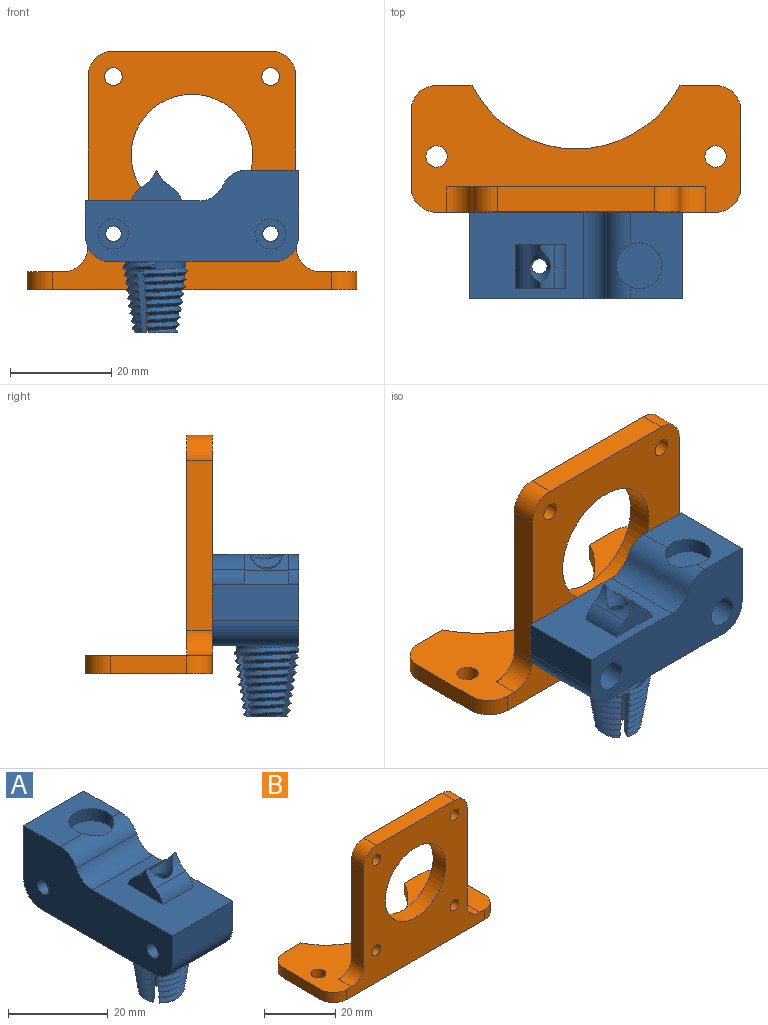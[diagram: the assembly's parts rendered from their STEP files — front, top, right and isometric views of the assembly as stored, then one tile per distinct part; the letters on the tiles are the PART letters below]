
ASSEMBLY  parts=2 mates=1
PART A: 93 faces, bbox 17.4x42.2x32.9 mm
  f0: plane 22.5x17mm, normal (0,0,1), area 296.5mm2, adj f61,f64,f66,f69,f72,f73,f85,f91
  f1: bspline ~12.95x12.81mm, area 38.6mm2, adj f2,f6,f9,f25,f76,f77,f78,f81
  f2: bspline ~12.93x12.82mm, area 52.3mm2, adj f1,f6,f40,f60,f79,f80,f81,f83
  f3: plane 32x17mm, normal (0,0,-1), area 430.9mm2, adj f7,f8,f60,f66,f85
  f4: cylinder r=3mm len=7mm, axis (1,0,0), area 131.9mm2, adj f67,f85
  f5: cylinder r=3mm len=7mm, axis (1,0,0), area 131.9mm2, adj f68,f85
  f6: plane 1.5x0.55mm, normal (0,1,0), area 0.4mm2, adj f1,f2,f60,f86
  f7: cylinder r=5mm len=17mm, axis (-1,0,0), area 133.5mm2, adj f3,f64,f66,f85
  f8: cylinder r=5mm len=17mm, axis (1,0,0), area 133.5mm2, adj f3,f65,f66,f85
  f9: bspline ~8.42x5.37mm, area 10.7mm2, adj f1,f33,f78,f81
  f10: bspline ~10.47x7.65mm, area 10.2mm2, adj f33,f34,f78,f81
  f11: bspline ~11.25x9.09mm, area 9.7mm2, adj f34,f35,f78,f81
  f12: bspline ~9.94x6.45mm, area 9.2mm2, adj f35,f36,f78,f81
  f13: bspline ~8.41x7.9mm, area 8.7mm2, adj f36,f37,f78,f81
  f14: bspline ~6.62x4.21mm, area 8.2mm2, adj f37,f38,f78,f81
  f15: bspline ~7.95x6.8mm, area 7.7mm2, adj f38,f39,f78,f81
  f16: bspline ~7.75x7.69mm, area 5.2mm2, adj f39,f57,f78,f81
  f17: bspline ~12.25x7.86mm, area 10.5mm2, adj f40,f41,f80,f83
  f18: bspline ~11.43x5.71mm, area 10mm2, adj f41,f42,f80,f83
  f19: bspline ~8.73x2.48mm, area 9.5mm2, adj f42,f43,f80,f83
  f20: bspline ~10.76x6.9mm, area 9mm2, adj f43,f44,f80,f83
  f21: bspline ~10.16x4.53mm, area 8.5mm2, adj f44,f45,f80,f83
  f22: bspline ~9.79x5.76mm, area 8mm2, adj f45,f46,f80,f83
  f23: bspline ~9.22x3.92mm, area 7.5mm2, adj f46,f47,f80,f83
  f24: bspline ~5.06x1.51mm, area 1mm2, adj f47,f58,f80
  f25: bspline ~12.58x9.49mm, area 10.8mm2, adj f1,f48,f77,f84
  f26: bspline ~10.93x7.22mm, area 10.3mm2, adj f48,f49,f77,f84
  f27: bspline ~7.78x5.02mm, area 9.8mm2, adj f49,f50,f77,f84
  f28: bspline ~9.75x7.21mm, area 9.3mm2, adj f50,f51,f77,f84
  f29: bspline ~10.36x8.84mm, area 8.8mm2, adj f51,f52,f77,f84
  f30: bspline ~8.65x7.04mm, area 8.3mm2, adj f52,f53,f77,f84
  f31: bspline ~9.22x8.3mm, area 7.8mm2, adj f53,f54,f77,f84
  f32: bspline ~7.52x6.72mm, area 7.3mm2, adj f54,f55,f77,f84
  f33: bspline ~8.42x5.4mm, area 10.5mm2, adj f9,f10,f78,f81
  f34: bspline ~8.06x5.17mm, area 10mm2, adj f10,f11,f78,f81
  f35: bspline ~7.7x4.94mm, area 9.5mm2, adj f11,f12,f78,f81
  f36: bspline ~7.34x4.71mm, area 9mm2, adj f12,f13,f78,f81
  f37: bspline ~6.98x4.47mm, area 8.5mm2, adj f13,f14,f78,f81
  f38: bspline ~6.62x4.24mm, area 8mm2, adj f14,f15,f78,f81
  f39: bspline ~6.26x4.01mm, area 7.5mm2, adj f15,f16,f78,f81
  f40: bspline ~9.97x2.98mm, area 10.8mm2, adj f2,f17,f80,f83
  f41: bspline ~9.56x2.86mm, area 10.3mm2, adj f17,f18,f80,f83
  f42: bspline ~9.14x2.75mm, area 9.8mm2, adj f18,f19,f80,f83
  f43: bspline ~8.73x2.63mm, area 9.3mm2, adj f19,f20,f80,f83
  f44: bspline ~8.31x2.52mm, area 8.8mm2, adj f20,f21,f80,f83
  f45: bspline ~7.9x2.4mm, area 8.3mm2, adj f21,f22,f80,f83
  f46: bspline ~7.48x2.29mm, area 7.8mm2, adj f22,f23,f80,f83
  f47: bspline ~7.06x2.18mm, area 7.3mm2, adj f23,f24,f58,f80,f83
  f48: bspline ~8.5x5.52mm, area 10.7mm2, adj f25,f26,f77,f84
  f49: bspline ~8.14x5.29mm, area 10.2mm2, adj f26,f27,f77,f84
  f50: bspline ~7.78x5.05mm, area 9.7mm2, adj f27,f28,f77,f84
  f51: bspline ~7.42x4.82mm, area 9.1mm2, adj f28,f29,f77,f84
  f52: bspline ~7.06x4.59mm, area 8.6mm2, adj f29,f30,f77,f84
  f53: bspline ~6.7x4.36mm, area 8.2mm2, adj f30,f31,f77,f84
  f54: bspline ~6.34x4.13mm, area 7.6mm2, adj f31,f32,f77,f84
  f55: bspline ~7.52x6.72mm, area 3.3mm2, adj f32,f59,f77,f84
  f56: cylinder r=2.2mm len=26mm, axis (0,0,1), area 304.3mm2, adj f57,f58,f59,f75,f76,f77,f78,f79
  f57: plane 5.91x3.58mm, normal (0,0,-1), area 11mm2, adj f16,f56,f78,f81
  f58: plane 6.05x2.29mm, normal (0,0,-1), area 8.2mm2, adj f24,f47,f56,f80,f83
  f59: plane 5.6x3.29mm, normal (0,0,-1), area 10.1mm2, adj f55,f56,f77,f84
  f60: cone r=6mm half-angle=9deg, axis (0,0,1), area 28.2mm2, adj f2,f3,f6
  f61: plane 10x6mm, normal (1,0,0), area 30.3mm2, adj f0,f70,f71,f72,f73
  f62: cylinder r=1.55mm len=10mm, axis (-1,0,0), area 97.4mm2, adj f66,f68
  f63: cylinder r=1.55mm len=10mm, axis (-1,0,0), area 97.4mm2, adj f66,f67
  f64: plane 17x7mm, normal (0,-1,0), area 119mm2, adj f0,f7,f66,f85
  f65: plane 17x13mm, normal (0,1,0), area 221mm2, adj f8,f66,f85,f88
  f66: plane 42x18mm, normal (-1,0,0), area 567.7mm2, adj f0,f3,f7,f8,f62,f63,f64,f65
  f67: plane 6x6mm, normal (1,0,0), area 20.7mm2, adj f4,f63
  f68: plane 6x6mm, normal (1,0,0), area 20.7mm2, adj f5,f62
  f69: plane 10x6mm, normal (-1,0,0), area 30.3mm2, adj f0,f70,f71,f72,f73
  f70: cylinder r=6.85mm len=8.6mm, axis (1,0,0), area 21.4mm2, adj f61,f69,f71,f73,f87
  f71: cylinder r=6.36mm len=8.6mm, axis (1,0,0), area 19.7mm2, adj f61,f69,f70,f72,f87
  f72: cylinder r=5mm len=8.6mm, axis (1,0,0), area 31.5mm2, adj f0,f61,f69,f71
  f73: cylinder r=5mm len=8.6mm, axis (1,0,0), area 31.8mm2, adj f0,f61,f69,f70
  f74: cylinder r=1.5mm len=3mm, axis (0,0,-1), area 18.8mm2, adj f75,f87
  f75: plane 4.4x4.4mm, normal (0,0,-1), area 8.1mm2, adj f56,f74
  f76: plane 4.26x1.51mm, normal (0,0,-1), area 6.2mm2, adj f1,f56,f77,f78
  f77: plane 12.02x4.19mm, normal (1,0,0), area 35.4mm2, adj f1,f25,f26,f27,f28,f29,f30,f31
  f78: plane 12.02x4.25mm, normal (-1,0,0), area 35.4mm2, adj f1,f9,f10,f11,f12,f13,f14,f15
  f79: plane 4.12x3.23mm, normal (0,0,-1), area 5.7mm2, adj f2,f56,f80,f81
  f80: plane 12.02x3.62mm, normal (0.5,0.87,0), area 35.5mm2, adj f2,f17,f18,f19,f20,f21,f22,f23
  f81: plane 12.02x3.63mm, normal (-0.5,-0.87,0), area 35.5mm2, adj f1,f2,f9,f10,f11,f12,f13,f14
  f82: plane 3.97x3.13mm, normal (0,0,-1), area 5.4mm2, adj f1,f56,f83,f84
  f83: plane 12.02x3.56mm, normal (-0.5,0.87,0), area 35.4mm2, adj f1,f2,f17,f18,f19,f20,f21,f22
  f84: plane 12.02x3.55mm, normal (0.5,-0.87,0), area 35.4mm2, adj f1,f25,f26,f27,f28,f29,f30,f31
  f85: plane 42x18mm, normal (1,0,0), area 526.2mm2, adj f0,f3,f4,f5,f7,f8,f64,f65
  f86: plane 1.9x0.78mm, normal (1,0,0), area 0.6mm2, adj f1,f2,f6
  f87: cone r=1.5mm half-angle=25deg, axis (0,0,1), area 27mm2, adj f70,f71,f74
  f88: plane 17x10.34mm, normal (0,0,1), area 128.2mm2, adj f65,f66,f85,f89,f92
  f89: cylinder r=4.5mm len=9mm, axis (0,0,1), area 84.8mm2, adj f88,f90,f92
  f90: plane 9x9mm, normal (0,0,1), area 63.6mm2, adj f89
  f91: cylinder r=5mm len=17mm, axis (1,0,0), area 98.5mm2, adj f0,f66,f85,f92
  f92: cylinder r=5mm len=17mm, axis (1,0,0), area 81.8mm2, adj f66,f85,f88,f89,f91
PART B: 29 faces, bbox 65x25x47 mm
  f0: plane 33.5x5mm, normal (-1,0,0), area 167.5mm2, adj f2,f5,f19,f25
  f1: plane 33.5x5mm, normal (1,0,0), area 167.5mm2, adj f2,f5,f20,f26
  f2: plane 51x43.5mm, normal (0,1,0), area 1292.6mm2, adj f0,f1,f3,f6,f7,f8,f9,f10
  f3: plane 31x5mm, normal (0,0,1), area 155mm2, adj f2,f5,f25,f26
  f4: plane 65x25mm, normal (0,0,-1), area 1209.6mm2, adj f5,f12,f13,f14,f15,f16,f17,f18
  f5: plane 55x47mm, normal (0,-1,0), area 1485.1mm2, adj f0,f1,f3,f4,f6,f7,f8,f9
  f6: cylinder r=12mm len=24mm, axis (0,-1,0), area 377mm2, adj f2,f5
  f7: cylinder r=1.75mm len=5mm, axis (0,-1,0), area 55mm2, adj f2,f5
  f8: cylinder r=1.75mm len=5mm, axis (0,-1,0), area 55mm2, adj f2,f5
  f9: cylinder r=1.75mm len=5mm, axis (0,-1,0), area 55mm2, adj f2,f5
  f10: cylinder r=1.75mm len=5mm, axis (0,-1,0), area 55mm2, adj f2,f5
  f11: plane 65x25mm, normal (0,0,1), area 954.6mm2, adj f2,f5,f12,f13,f14,f15,f16,f17
  f12: plane 15x3.5mm, normal (1,0,0), area 52.5mm2, adj f4,f11,f23,f24
  f13: plane 15x3.5mm, normal (-1,0,0), area 52.5mm2, adj f4,f11,f21,f22
  f14: plane 7x3.5mm, normal (0,1,0), area 24.5mm2, adj f4,f11,f17,f22
  f15: plane 3.5x0.07mm, normal (0,1,0), area 0.3mm2, adj f4,f11,f17,f18
  f16: plane 7x3.5mm, normal (0,1,0), area 24.5mm2, adj f4,f11,f18,f23
  f17: cylinder r=23mm len=20.46mm, axis (0,0,1), area 88.3mm2, adj f4,f11,f14,f15
  f18: cylinder r=23mm len=20.46mm, axis (0,0,-1), area 88.3mm2, adj f4,f11,f15,f16
  f19: cylinder r=5mm len=5mm, axis (0,-1,0), area 39.3mm2, adj f0,f2,f5,f11
  f20: cylinder r=5mm len=5mm, axis (0,1,0), area 39.3mm2, adj f1,f2,f5,f11
  f21: cylinder r=5mm len=5mm, axis (0,0,-1), area 27.5mm2, adj f4,f5,f11,f13
  f22: cylinder r=5mm len=5mm, axis (0,0,-1), area 27.5mm2, adj f4,f11,f13,f14
  f23: cylinder r=5mm len=5mm, axis (0,0,1), area 27.5mm2, adj f4,f11,f12,f16
  f24: cylinder r=5mm len=5mm, axis (0,0,1), area 27.5mm2, adj f4,f5,f11,f12
  f25: cylinder r=5mm len=5mm, axis (0,-1,0), area 39.3mm2, adj f0,f2,f3,f5
  f26: cylinder r=5mm len=5mm, axis (0,1,0), area 39.3mm2, adj f1,f2,f3,f5
  f27: cylinder r=2.1mm len=4.2mm, axis (0,0,1), area 46.2mm2, adj f4,f11
  f28: cylinder r=2.1mm len=4.2mm, axis (0,0,1), area 46.2mm2, adj f4,f11
PLACE A rot(axis=(0,0,-1),90deg) t=(0,-14,13)mm
PLACE B at identity
MATE fastened A.f4 <-> B.f9  axis (0,1,0) through (-15.5,-5,11)mm
